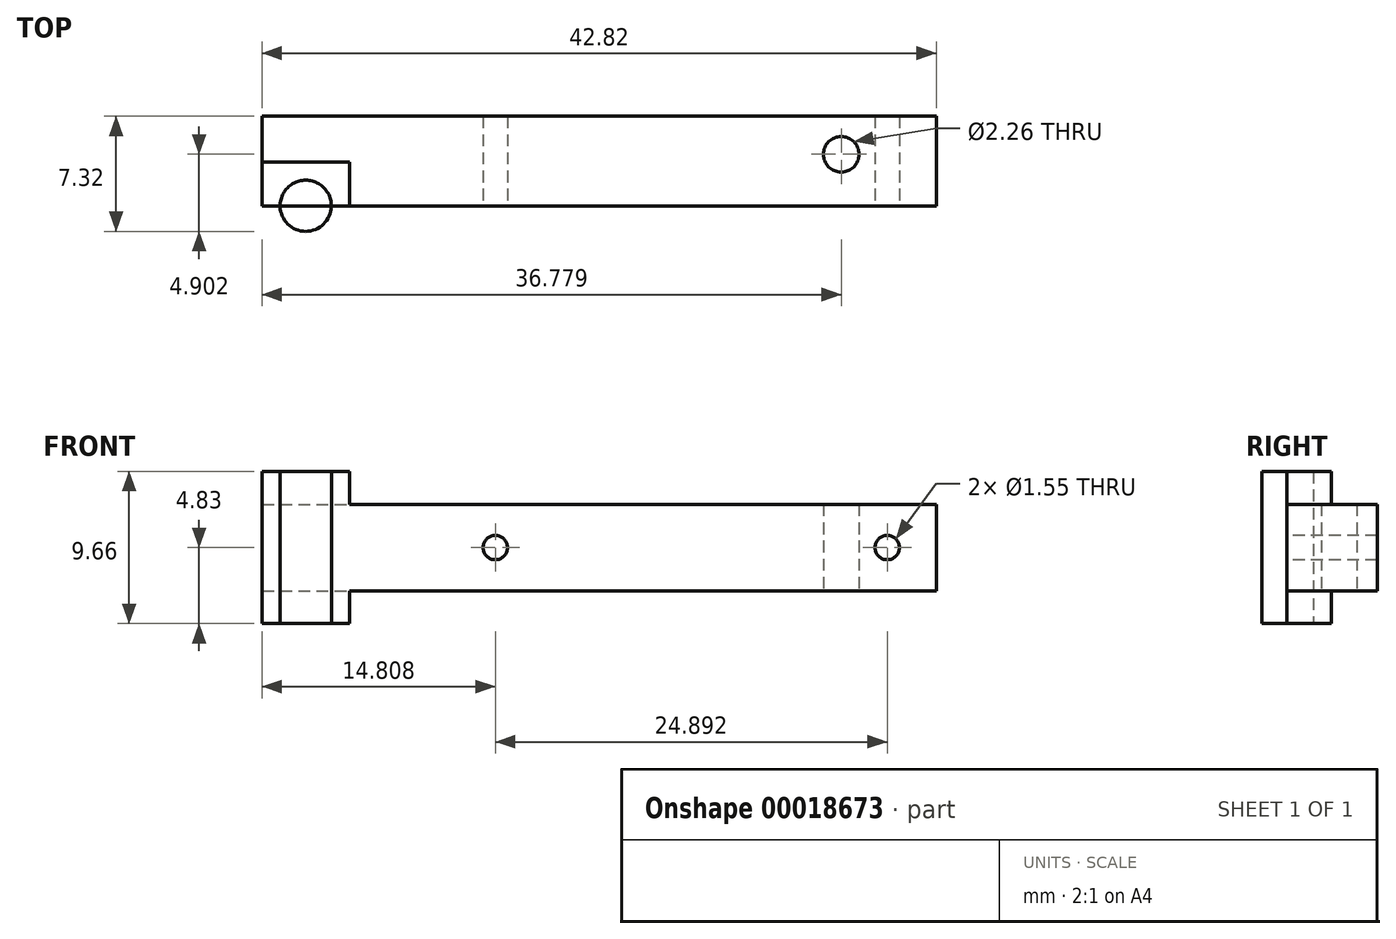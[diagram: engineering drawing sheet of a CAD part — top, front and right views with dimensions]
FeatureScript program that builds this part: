
annotation { "Feature Type Name" : "Feature", "Feature Type Description" : "" }
export const myFeature = defineFeature(function(context is Context, id is Id, definition is map)
    precondition{}
    {
        {
            var Q0;
            Q0=qCreatedBy(makeId("Top.planeOp"),FACE);
            var sketch = newSketch(context, id + "F0", { "sketchPlane" : qUnion([Q0])});
            skLineSegment(sketch, "E0", {"start": v(0, 0) * mm, "end": v(0, 44.42) * mm, "construction": true});
            skLineSegment(sketch, "E1.bottom", {"start": v(0, 0) * mm, "end": v(42.82, 0) * mm});
            skLineSegment(sketch, "E1.left", {"start": v(0, 0) * mm, "end": v(0, 4.65) * mm});
            skLineSegment(sketch, "E1.right", {"start": v(42.82, 0) * mm, "end": v(42.82, 4.65) * mm});
            skLineSegment(sketch, "E2", {"start": v(-26.81, 3.3) * mm, "end": v(59.5, 3.3) * mm, "construction": true});
            skCircle(sketch, "E3", {"center": v(36.78, 3.3) * mm, "radius": 1.13 * mm});
            skCircle(sketch, "E4.0", {"center": v(2.77, 0.03) * mm, "radius": 1.63 * mm});
            skLineSegment(sketch, "E5.bottom", {"start": v(0, 5.72) * mm, "end": v(42.82, 5.72) * mm});
            skLineSegment(sketch, "E5.top", {"start": v(0, -2.74) * mm, "end": v(5.54, -2.74) * mm});
            skLineSegment(sketch, "E5.left", {"start": v(0, 5.72) * mm, "end": v(0, -2.74) * mm});
            skLineSegment(sketch, "E5.right", {"start": v(42.82, 5.72) * mm, "end": v(42.82, 0) * mm});
            skLineSegment(sketch, "E6.bottom", {"start": v(5.54, 0) * mm, "end": v(42.82, 0) * mm});
            skLineSegment(sketch, "E6.top", {"start": v(5.54, -2.74) * mm, "end": v(5.54, -2.74) * mm});
            skLineSegment(sketch, "E7.top", {"start": v(0, 2.8) * mm, "end": v(5.54, 2.8) * mm});
            skLineSegment(sketch, "E7.left", {"start": v(0, -2.74) * mm, "end": v(0, 2.8) * mm});
            skLineSegment(sketch, "E7.right", {"start": v(5.54, -2.74) * mm, "end": v(5.54, 2.8) * mm});
            skSolve(sketch);
        }
        {
            var Q0;
            Q0=makeQuery(id+"F0.imprint","IMPRINT",FACE,{"disambiguationData":[TD([[makeQuery(id+"F0.imprint","IMPRINT",EDGE,{"derivedFrom":sQuery(id+"F0.wireOp",EDGE,"E3")}),-1.0]])]});
            extrude(context, id + "F1", {"entities" : qUnion([Q0]), "endBound" : BoundingType.SYMMETRIC, "depth" : 5.5 * mm});
        }
        {
            var Q0;
            {var subQ1=sQuery(id+"F0.wireOp",EDGE,"E7.top");Q0=makeQuery(id+"F0.imprint","IMPRINT",FACE,{"disambiguationData":[TD([[makeQuery(id+"F0.imprint","IMPRINT",EDGE,{"derivedFrom":subQ1}),-1.0]])]});}
            var Q1;
            {var subQ5=sQuery(id+"F0.wireOp",EDGE,"E7.left");var subQ7=sQuery(id+"F0.wireOp",EDGE,"E1.bottom");var subQ8=makeQuery(id+"F0.imprint","INTERSECT",VERTEX,{"derivedFrom":[subQ7,subQ5]});Q1=makeQuery(id+"F0.imprint","IMPRINT",FACE,{"disambiguationData":[TD([[makeQuery(id+"F0.imprint","IMPRINT",EDGE,{"disambiguationData":[TD([[subQ8,-1.0]])],"derivedFrom":subQ7}),-1.0]])]});}
            extrude(context, id + "F2", {"entities" : qUnion([Q0, Q1]), "operationType" : NewBodyOperationType.ADD, "endBound" : BoundingType.SYMMETRIC, "depth" : 9.65 * mm});
        }
        {
            var Q0;
            Q0=qCreatedBy(makeId("Front.planeOp"),FACE);
            var sketch = newSketch(context, id + "F3", { "sketchPlane" : qUnion([Q0])});
            skCircle(sketch, "E8", {"center": v(14.8, 0) * mm, "radius": 0.77 * mm});
            skCircle(sketch, "E9", {"center": v(39.7, 0) * mm, "radius": 0.77 * mm});
            skSolve(sketch);
        }
        {
            var Q0;
            Q0=makeQuery(id+"F3.imprint","IMPRINT",FACE,{"disambiguationData":[TD([[makeQuery(id+"F3.imprint","IMPRINT",EDGE,{"derivedFrom":sQuery(id+"F3.wireOp",EDGE,"E9")}),1.0]])]});
            var Q1;
            Q1=makeQuery(id+"F3.imprint","IMPRINT",FACE,{"disambiguationData":[TD([[makeQuery(id+"F3.imprint","IMPRINT",EDGE,{"derivedFrom":sQuery(id+"F3.wireOp",EDGE,"E8")}),1.0]])]});
            extrude(context, id + "F4", {"entities" : qUnion([Q0, Q1]), "operationType" : NewBodyOperationType.REMOVE, "oppositeDirection" : true, "depth" : 25.4 * mm});
        }
    });
